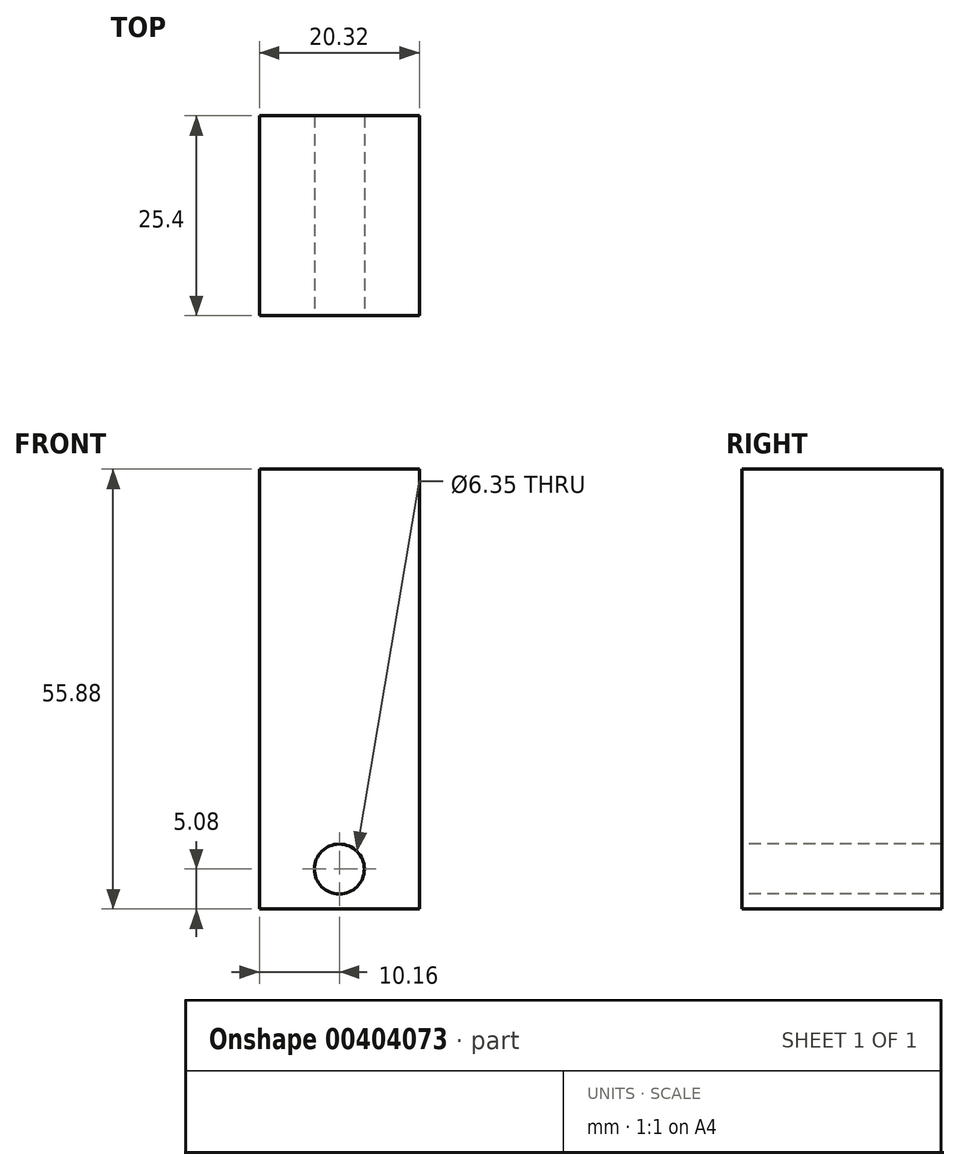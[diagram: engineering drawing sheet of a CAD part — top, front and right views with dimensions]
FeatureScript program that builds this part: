
annotation { "Feature Type Name" : "Feature", "Feature Type Description" : "" }
export const myFeature = defineFeature(function(context is Context, id is Id, definition is map)
    precondition{}
    {
        {
            var Q0;
            Q0=qCreatedBy(makeId("Front.planeOp"),FACE);
            var sketch = newSketch(context, id + "F0", { "sketchPlane" : qUnion([Q0])});
            skLineSegment(sketch, "E0.bottom", {"start": v(10.16, 27.94) * mm, "end": v(-10.16, 27.94) * mm});
            skLineSegment(sketch, "E0.top", {"start": v(10.16, -27.94) * mm, "end": v(-10.16, -27.94) * mm});
            skLineSegment(sketch, "E0.left", {"start": v(10.16, 27.94) * mm, "end": v(10.16, -27.94) * mm});
            skLineSegment(sketch, "E0.right", {"start": v(-10.16, 27.94) * mm, "end": v(-10.16, -27.94) * mm});
            skPoint(sketch, "E0.middle", {"position": v(0, 0) * mm});
            skSolve(sketch);
        }
        {
            var Q0;
            Q0=makeQuery(id+"F0.imprint","IMPRINT",FACE,{"disambiguationData":[TD([[makeQuery(id+"F0.imprint","IMPRINT",EDGE,{"derivedFrom":sQuery(id+"F0.wireOp",EDGE,"E0.bottom")}),1.0]])]});
            extrude(context, id + "F1", {"entities" : qUnion([Q0]), "depth" : 25.4 * mm});
        }
        {
            var Q0;
            Q0=makeQuery(id+"F1.opExtrude","CAP_FACE",FACE,{"disambiguationData":[OSD([sQuery(id+"F0.wireOp",EDGE,"E0.bottom"),sQuery(id+"F0.wireOp",EDGE,"E0.top"),sQuery(id+"F0.wireOp",EDGE,"E0.left"),sQuery(id+"F0.wireOp",EDGE,"E0.right")])],"isStart":false});
            var sketch = newSketch(context, id + "F2", { "sketchPlane" : qUnion([Q0])});
            skCircle(sketch, "E1", {"center": v(0, -22.86) * mm, "radius": 3.18 * mm});
            skSolve(sketch);
        }
        {
            var Q0;
            Q0=makeQuery(id+"F2.imprint","IMPRINT",FACE,{"disambiguationData":[TD([[makeQuery(id+"F2.imprint","IMPRINT",EDGE,{"derivedFrom":sQuery(id+"F2.wireOp",EDGE,"E1")}),1.0]])]});
            extrude(context, id + "F3", {"entities" : qUnion([Q0]), "operationType" : NewBodyOperationType.REMOVE, "endBound" : BoundingType.THROUGH_ALL, "oppositeDirection" : true, "depth" : 25.4 * mm});
        }
    });
